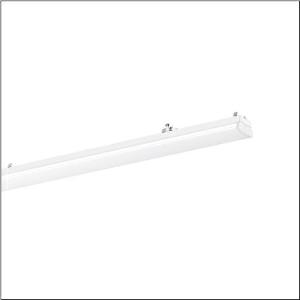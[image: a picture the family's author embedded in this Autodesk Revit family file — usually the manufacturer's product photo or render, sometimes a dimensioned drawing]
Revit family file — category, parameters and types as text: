
# Revit family: licross_r__11_recessed_opal_mo_51tl1ddn445g_7b5e
name_source: partatom
category: Lighting Fixtures
units: mm (PartAtom-declared; Revit-internal decimal feet)

## family parameters
Cut with Voids When Loaded = No
Host = Face
Light Source = No
Part Type = Normal
Room Calculation Point = No
Round Connector Dimension = Use Diameter
Shared = No

## types (1)
- --- (1 x LED, 4500 lm, 25.2 W, 4000K)
    Apparent Load = 25 VA
    CIE Flux Codes = 44 73 91 87 100
    Color Rendering = 80
    Color Temperature = 4000K
    Default Elevation = 1800 mm
    Description = Licross® 11 recessed opal MO, luminaire insert, of sheet steel, coil coated, white, length: 1.500mm, width: 76mm, height: 87mm, LED rated luminous flux: 4.500lm, light colour: 840, control gear: DALI 2, with plug, 5-pole, with phase selection, mains connection: 220..240V, AC, 50/60Hz, rated input power: 25W, halogen-free wiring, primary optical cover: cover, of PMMA, light emission: direct with ceiling illumination distribution, primary light characteristic: symmetric, protection rating (complete): IP40, insulation class (complete): insulation class I (protective earthing), certification: CE, ENEC, VDE, UKCA, protection symbol: D if used in an environment without relevant dust loads with corresponding accessories, impact resistance: IK06, permissible ambient temperature for indoor applications: -25..+45°C, corresponds to IFS (International Featured Standards) requirements for safety and quality in the food industry, reducing of maximum allowable ambient temperature of 5°C with ceiling mounting, LABS conformity tested according to VDMA 24364:2018-05, packaging unit: 1 piece
    Height = 83 mm
    Lamp = 1 x LED
    Lamp Light Flux = 4500 lm
    Lamp Power = 25.2 W
    Lamp count = 1
    Length = 1500 mm
    Luminous efficacy = 179 lm/W
    Manufacturer = Siteco
    ModVariant = No
    Model = 51TL1DDN445G
    Mounting Place = Ceiling
    Mounting Type = Pendant
    Number of Poles = 1
    OnlyDefault = Yes
    Power Factor = 1
    Product Name = Licross® 11 recessed opal MO
    Product group = luminaire insert
    ProductGroupID = 901
    Protection Class = Protection class I
    Protection Degree = IP 40
    RLX_Detail_Level = 1
    RLX_Emergency_Light_Flux = 0 lm
    RLX_Emergency_Type = 0
    RLX_Emergency_Type_DB = No
    RlxData = <blob elided: 17853 chars, md5=fd155c50>
    Socket = socket
    Standby Power = 0 W
    System Light Flux = 4500 lm
    System Power = 25 W
    Type Comments = factory setting: luminous flux: 100 % | dim-lin: 254 | 167 mA
    Type Image = l_1313666.jpg
    URL = http://relux.com
    VarID = @adj_027471
    Voltage = 0 V
    Weight = 0.00 kg
    Width = 76 mm

## geometry (parser evidence)
native form markers: Blend x4, Sweep x12
no freeform markers — native parametric forms only
